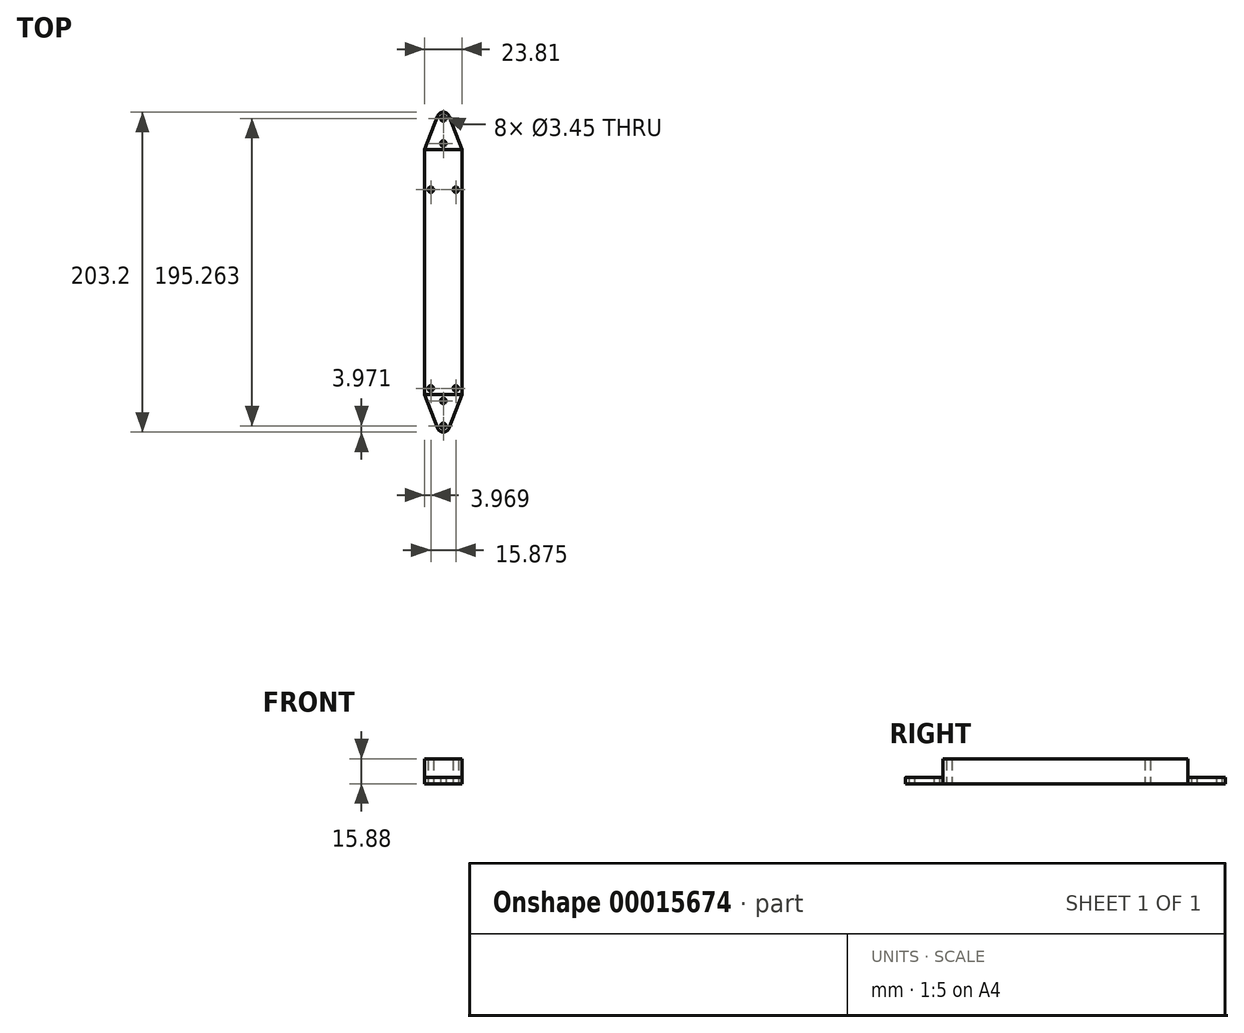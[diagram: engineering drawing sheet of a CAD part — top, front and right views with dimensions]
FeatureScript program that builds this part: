
annotation { "Feature Type Name" : "Feature", "Feature Type Description" : "" }
export const myFeature = defineFeature(function(context is Context, id is Id, definition is map)
    precondition{}
    {
        {
            var Q0;
            Q0=qCreatedBy(makeId("Top.planeOp"),FACE);
            var sketch = newSketch(context, id + "F0", { "sketchPlane" : qUnion([Q0])});
            skLineSegment(sketch, "E0.bottom", {"start": v(0, 0) * mm, "end": v(23.81, 0) * mm, "construction": true});
            skLineSegment(sketch, "E0.top", {"start": v(0, -155.58) * mm, "end": v(23.81, -155.58) * mm, "construction": true});
            skLineSegment(sketch, "E0.left", {"start": v(0, 0) * mm, "end": v(0, -155.58) * mm});
            skLineSegment(sketch, "E0.right", {"start": v(23.81, 0) * mm, "end": v(23.81, -155.58) * mm});
            skLineSegment(sketch, "E1", {"start": v(3.97, -151.6) * mm, "end": v(11.9, -151.6) * mm});
            skLineSegment(sketch, "E2", {"start": v(11.9, -151.6) * mm, "end": v(19.84, -151.6) * mm, "construction": true});
            skCircle(sketch, "E3", {"center": v(3.97, -151.6) * mm, "radius": 1.73 * mm});
            skCircle(sketch, "E4", {"center": v(19.84, -151.6) * mm, "radius": 1.73 * mm});
            skLineSegment(sketch, "E5", {"start": v(11.9, -155.58) * mm, "end": v(11.9, -159.54) * mm});
            skLineSegment(sketch, "E6", {"start": v(11.9, -159.54) * mm, "end": v(11.9, -167.48) * mm});
            skLineSegment(sketch, "E7", {"start": v(11.9, -167.48) * mm, "end": v(11.9, -175.42) * mm});
            skLineSegment(sketch, "E8", {"start": v(11.9, -175.42) * mm, "end": v(11.9, -179.39) * mm});
            skLineSegment(sketch, "E9", {"start": v(0, -155.58) * mm, "end": v(8.2, -176.85) * mm});
            skLineSegment(sketch, "E10", {"start": v(23.81, -155.58) * mm, "end": v(15.6, -176.85) * mm});
            skArc(sketch, "E11", {"start": v(8.2, -176.85) * mm, "mid": v(11.9, -179.39) * mm, "end": v(15.6, -176.85) * mm});
            skCircle(sketch, "E12", {"center": v(11.9, -175.42) * mm, "radius": 1.73 * mm});
            skCircle(sketch, "E13", {"center": v(11.9, -159.54) * mm, "radius": 1.73 * mm});
            skLineSegment(sketch, "E14", {"start": v(11.9, 0) * mm, "end": v(11.9, 3.97) * mm, "construction": true});
            skLineSegment(sketch, "E15", {"start": v(11.9, 3.97) * mm, "end": v(11.9, 11.9) * mm, "construction": true});
            skLineSegment(sketch, "E16", {"start": v(11.9, 11.9) * mm, "end": v(11.9, 19.84) * mm, "construction": true});
            skLineSegment(sketch, "E17", {"start": v(11.9, 19.84) * mm, "end": v(11.9, 23.81) * mm, "construction": true});
            skArc(sketch, "E18", {"start": v(15.6, 21.27) * mm, "mid": v(11.9, 23.81) * mm, "end": v(8.2, 21.27) * mm});
            skLineSegment(sketch, "E19", {"start": v(0, 0) * mm, "end": v(8.2, 21.27) * mm});
            skLineSegment(sketch, "E20", {"start": v(15.6, 21.27) * mm, "end": v(23.81, 0) * mm});
            skCircle(sketch, "E21", {"center": v(11.9, 19.84) * mm, "radius": 1.73 * mm});
            skCircle(sketch, "E22", {"center": v(11.9, 3.97) * mm, "radius": 1.73 * mm});
            skLineSegment(sketch, "E23", {"start": v(11.9, -151.6) * mm, "end": v(11.9, -155.58) * mm});
            skLineSegment(sketch, "E24", {"start": v(11.9, 0) * mm, "end": v(11.9, -25.4) * mm});
            skLineSegment(sketch, "E25", {"start": v(3.97, -25.4) * mm, "end": v(19.84, -25.4) * mm});
            skCircle(sketch, "E26", {"center": v(3.97, -25.4) * mm, "radius": 1.73 * mm});
            skCircle(sketch, "E27", {"center": v(19.84, -25.4) * mm, "radius": 1.73 * mm});
            skSolve(sketch);
        }
        {
            var Q0;
            Q0=qSketchRegion(id+"F0",true);
            extrude(context, id + "F1", {"entities" : qUnion([Q0]), "depth" : 3.97 * mm});
        }
        {
            var Q0;
            Q0=makeQuery(id+"F1.opExtrude","CAP_FACE",FACE,{"disambiguationData":[OSD([sQuery(id+"F0.wireOp",EDGE,"E0.left"),sQuery(id+"F0.wireOp",EDGE,"E0.right"),sQuery(id+"F0.wireOp",EDGE,"E3"),sQuery(id+"F0.wireOp",EDGE,"E4"),sQuery(id+"F0.wireOp",EDGE,"E9"),sQuery(id+"F0.wireOp",EDGE,"E10"),sQuery(id+"F0.wireOp",EDGE,"E11"),sQuery(id+"F0.wireOp",EDGE,"E12"),sQuery(id+"F0.wireOp",EDGE,"E13"),sQuery(id+"F0.wireOp",EDGE,"E18"),sQuery(id+"F0.wireOp",EDGE,"E19"),sQuery(id+"F0.wireOp",EDGE,"E20"),sQuery(id+"F0.wireOp",EDGE,"E21"),sQuery(id+"F0.wireOp",EDGE,"E22")])],"isStart":false});
            var sketch = newSketch(context, id + "F2", { "sketchPlane" : qUnion([Q0])});
            skLineSegment(sketch, "E28.bottom", {"start": v(0, -155.58) * mm, "end": v(23.81, -155.58) * mm});
            skLineSegment(sketch, "E28.top", {"start": v(0, 0) * mm, "end": v(23.81, 0) * mm});
            skLineSegment(sketch, "E28.left", {"start": v(0, -155.58) * mm, "end": v(0, 0) * mm});
            skLineSegment(sketch, "E28.right", {"start": v(23.81, -155.58) * mm, "end": v(23.81, 0) * mm});
            skSolve(sketch);
        }
        {
            var Q0;
            Q0=makeQuery(id+"F2.imprint","IMPRINT",FACE,{"disambiguationData":[TD([[makeQuery(id+"F2.imprint","IMPRINT",EDGE,{"derivedFrom":sQuery(id+"F2.wireOp",EDGE,"E28.bottom")}),1.0]])]});
            extrude(context, id + "F3", {"entities" : qUnion([Q0]), "operationType" : NewBodyOperationType.ADD, "depth" : 11.9 * mm});
        }
    });
